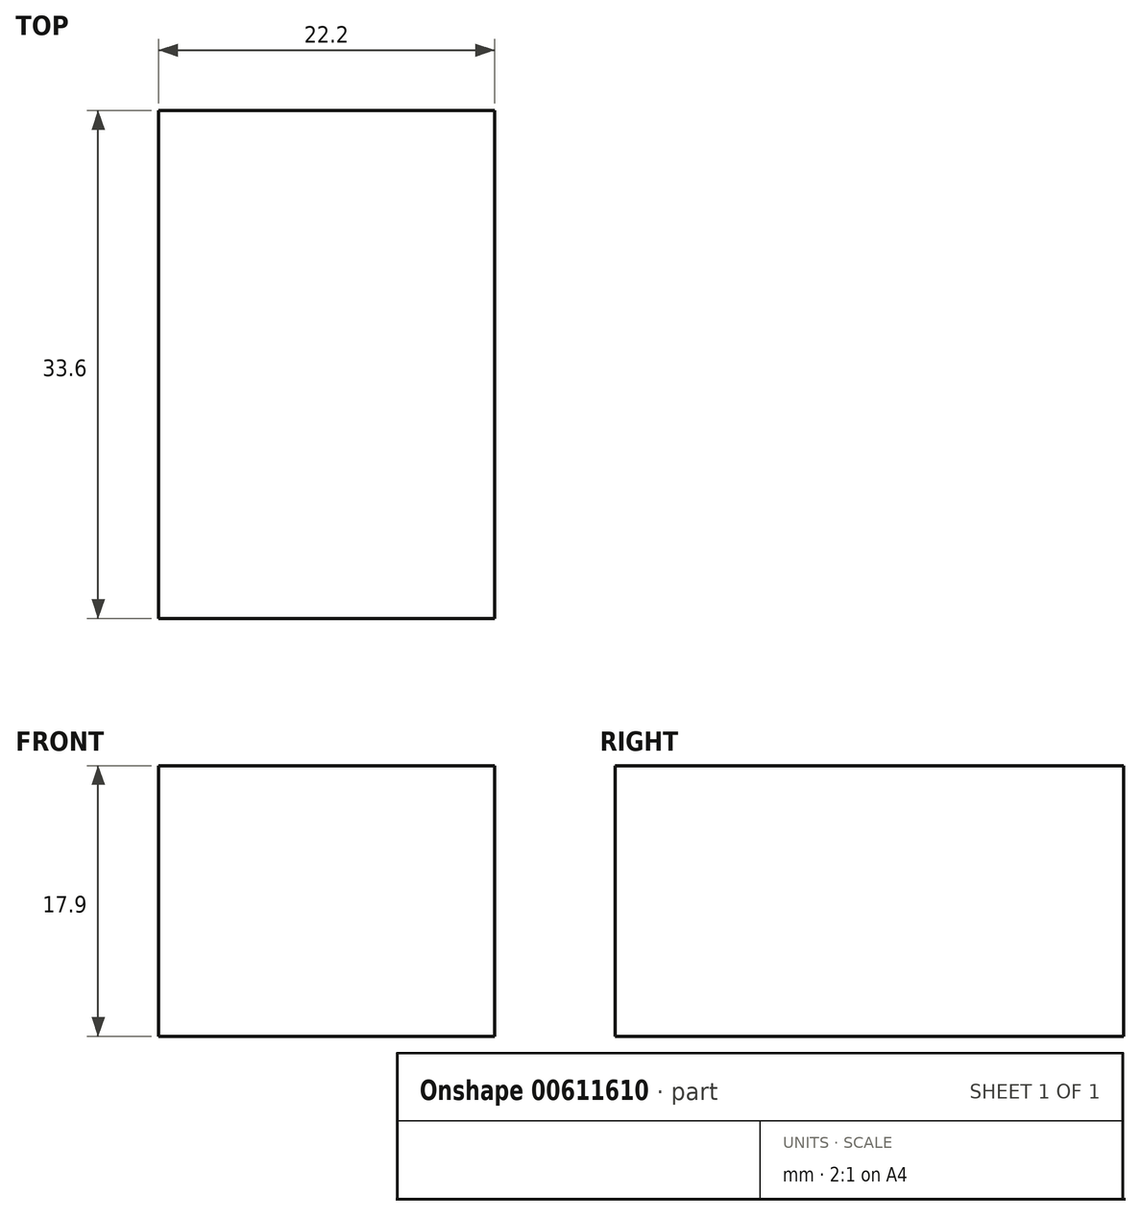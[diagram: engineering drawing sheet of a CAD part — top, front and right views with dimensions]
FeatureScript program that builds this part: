
annotation { "Feature Type Name" : "Feature", "Feature Type Description" : "" }
export const myFeature = defineFeature(function(context is Context, id is Id, definition is map)
    precondition{}
    {
        {
            var Q0;
            Q0=qCreatedBy(makeId("Top.planeOp"),FACE);
            var sketch = newSketch(context, id + "F0", { "sketchPlane" : qUnion([Q0])});
            skLineSegment(sketch, "E0.bottom", {"start": v(2.54, 36.14) * mm, "end": v(24.74, 36.14) * mm});
            skLineSegment(sketch, "E0.top", {"start": v(2.54, 2.54) * mm, "end": v(24.74, 2.54) * mm});
            skLineSegment(sketch, "E0.left", {"start": v(2.54, 36.14) * mm, "end": v(2.54, 2.54) * mm});
            skLineSegment(sketch, "E0.right", {"start": v(24.74, 36.14) * mm, "end": v(24.74, 2.54) * mm});
            skSolve(sketch);
        }
        {
            var Q0;
            Q0 = qSketchRegion(id + "F0", true);
            extrude(context, id + "F1", {"entities" : qUnion([Q0]), "depth" : 17.9 * mm, "offsetDistance" : 25 * mm});
        }
    });
